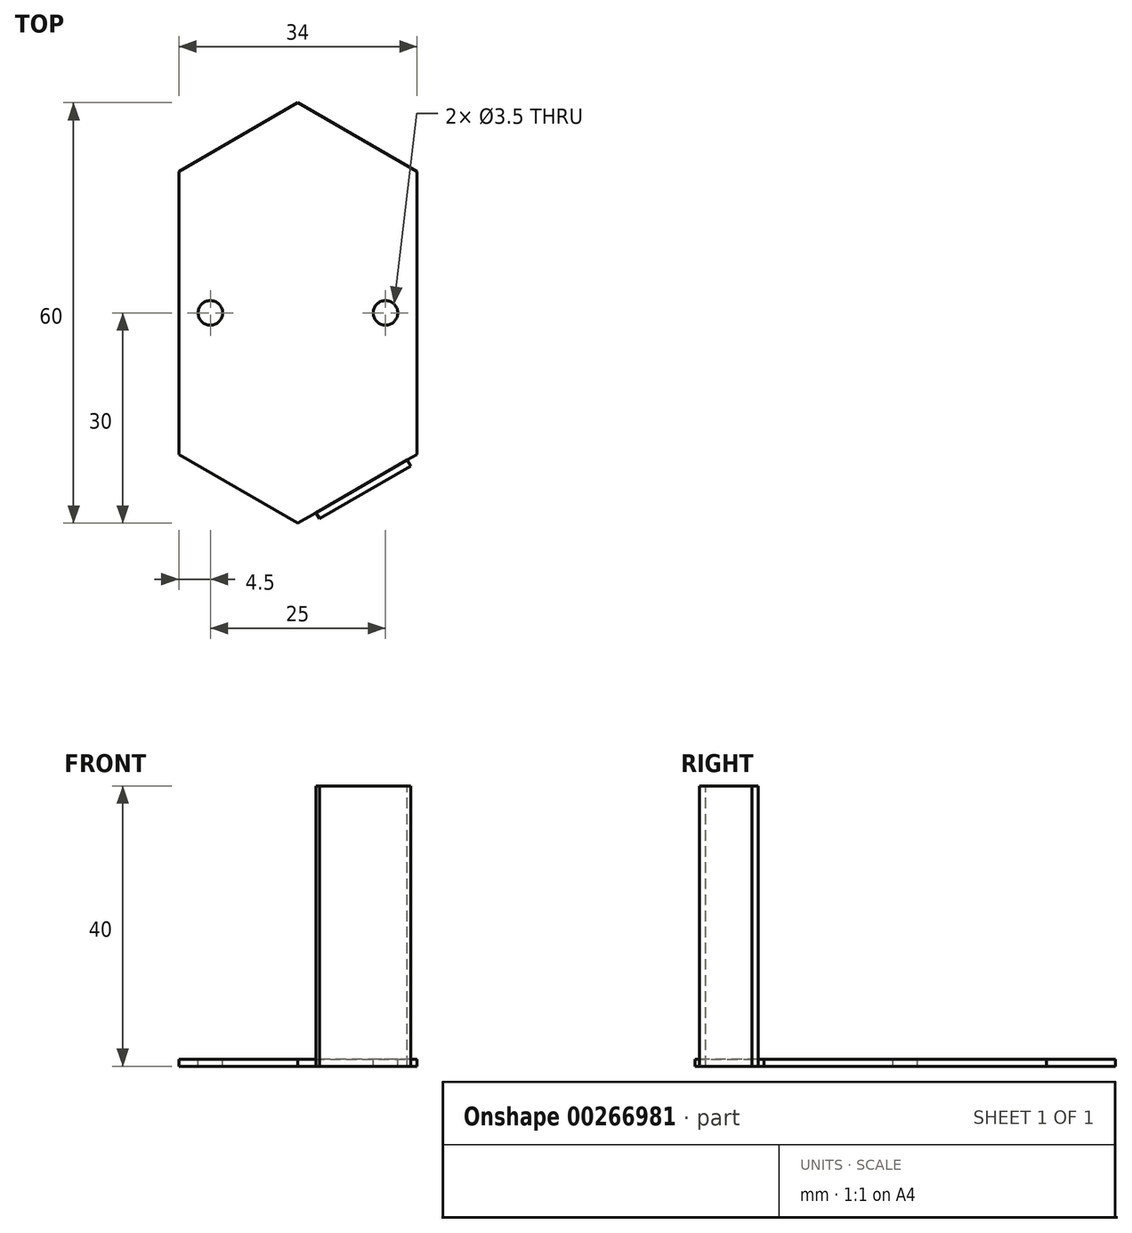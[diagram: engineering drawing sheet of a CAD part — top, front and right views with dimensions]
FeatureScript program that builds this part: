
annotation { "Feature Type Name" : "Feature", "Feature Type Description" : "" }
export const myFeature = defineFeature(function(context is Context, id is Id, definition is map)
    precondition{}
    {
        {
            var Q0;
            Q0=qCreatedBy(makeId("Top.planeOp"),FACE);
            var sketch = newSketch(context, id + "F0", { "sketchPlane" : qUnion([Q0])});
            skCircle(sketch, "E0.cCircle", {"center": v(0, 0) * mm, "radius": 25.98 * mm, "construction": true});
            skLineSegment(sketch, "E0.0", {"start": v(25.98, 15) * mm, "end": v(25.98, -15) * mm});
            skLineSegment(sketch, "E0.1", {"start": v(25.98, -15) * mm, "end": v(0, -30) * mm});
            skLineSegment(sketch, "E0.2", {"start": v(0, -30) * mm, "end": v(-25.98, -15) * mm});
            skLineSegment(sketch, "E0.3", {"start": v(-25.98, -15) * mm, "end": v(-25.98, 15) * mm});
            skLineSegment(sketch, "E0.4", {"start": v(-25.98, 15) * mm, "end": v(0, 30) * mm});
            skLineSegment(sketch, "E0.5", {"start": v(0, 30) * mm, "end": v(25.98, 15) * mm});
            skPoint(sketch, "E0.0.midPoint", {"position": v(25.98, 0) * mm});
            skSolve(sketch);
        }
        {
            var Q0;
            Q0 = qSketchRegion(id + "F0", true);
            extrude(context, id + "F1", {"entities" : qUnion([Q0]), "depth" : 1 * mm});
        }
        {
            var Q0;
            Q0=makeQuery(id+"F1.opExtrude","SWEPT_FACE",FACE,{"disambiguationData":[OSD([sQuery(id+"F0.wireOp",EDGE,"E0.1")])]});
            var sketch = newSketch(context, id + "F2", { "sketchPlane" : qUnion([Q0])});
            skLineSegment(sketch, "E1.bottom", {"start": v(-12, 0) * mm, "end": v(3, 0) * mm});
            skLineSegment(sketch, "E1.top", {"start": v(-12, 40) * mm, "end": v(3, 40) * mm});
            skLineSegment(sketch, "E1.left", {"start": v(-12, 0) * mm, "end": v(-12, 40) * mm});
            skLineSegment(sketch, "E1.right", {"start": v(3, 0) * mm, "end": v(3, 40) * mm});
            skSolve(sketch);
        }
        {
            var Q0;
            Q0 = qSketchRegion(id + "F2", true);
            extrude(context, id + "F3", {"entities" : qUnion([Q0]), "depth" : 1 * mm});
        }
        {
            var Q0;
            Q0=makeQuery(id+"F1.opExtrude","CAP_FACE",FACE,{"disambiguationData":[OSD([sQuery(id+"F0.wireOp",EDGE,"E0.0"),sQuery(id+"F0.wireOp",EDGE,"E0.1"),sQuery(id+"F0.wireOp",EDGE,"E0.2"),sQuery(id+"F0.wireOp",EDGE,"E0.3"),sQuery(id+"F0.wireOp",EDGE,"E0.4"),sQuery(id+"F0.wireOp",EDGE,"E0.5")])],"isStart":false});
            var sketch = newSketch(context, id + "F4", { "sketchPlane" : qUnion([Q0])});
            skLineSegment(sketch, "E2.bottom", {"start": v(-32, 25) * mm, "end": v(-17, 25) * mm});
            skLineSegment(sketch, "E2.top", {"start": v(-32, -25) * mm, "end": v(-17, -25) * mm});
            skLineSegment(sketch, "E2.left", {"start": v(-32, 25) * mm, "end": v(-32, -25) * mm});
            skLineSegment(sketch, "E2.right", {"start": v(-17, 25) * mm, "end": v(-17, -25) * mm});
            skLineSegment(sketch, "E3.MirrorCS", {"start": v(32, 25) * mm, "end": v(17, 25) * mm});
            skLineSegment(sketch, "E4.MirrorCS", {"start": v(32, -25) * mm, "end": v(17, -25) * mm});
            skLineSegment(sketch, "E5.MirrorCS", {"start": v(17, 25) * mm, "end": v(17, -25) * mm});
            skLineSegment(sketch, "E6.MirrorCS", {"start": v(32, 25) * mm, "end": v(32, -25) * mm});
            skSolve(sketch);
        }
        {
            var Q0;
            Q0 = qSketchRegion(id + "F4", true);
            extrude(context, id + "F5", {"entities" : qUnion([Q0]), "operationType" : NewBodyOperationType.REMOVE, "oppositeDirection" : true, "depth" : 25 * mm});
        }
        {
            var Q0;
            Q0=makeQuery(id+"F1.opExtrude","CAP_FACE",FACE,{"disambiguationData":[OSD([sQuery(id+"F0.wireOp",EDGE,"E0.0"),sQuery(id+"F0.wireOp",EDGE,"E0.1"),sQuery(id+"F0.wireOp",EDGE,"E0.2"),sQuery(id+"F0.wireOp",EDGE,"E0.3"),sQuery(id+"F0.wireOp",EDGE,"E0.4"),sQuery(id+"F0.wireOp",EDGE,"E0.5")])],"isStart":false});
            var sketch = newSketch(context, id + "F6", { "sketchPlane" : qUnion([Q0])});
            skPoint(sketch, "E7", {"position": v(12.5, 0) * mm});
            skPoint(sketch, "E8", {"position": v(-12.5, 0) * mm});
            skSolve(sketch);
        }
        {
            var Q0;
            Q0=sQuery(id+"F6.wireOp",VERTEX,"E7");
            var Q1;
            Q1=sQuery(id+"F6.wireOp",VERTEX,"E8");
            var Q2;
            Q2=makeQuery(id+"F1.opExtrude","SWEPT_BODY",BODY,{"disambiguationData":[OSD([sQuery(id+"F0.wireOp",EDGE,"E0.0"),sQuery(id+"F0.wireOp",EDGE,"E0.1"),sQuery(id+"F0.wireOp",EDGE,"E0.2"),sQuery(id+"F0.wireOp",EDGE,"E0.3"),sQuery(id+"F0.wireOp",EDGE,"E0.4"),sQuery(id+"F0.wireOp",EDGE,"E0.5")])]});
            hole(context, id + "F7", {"style" : HoleStyle.SIMPLE, "endStyle" : HoleEndStyle.THROUGH, "holeDiameter" : 3.5 * mm, "tappedDepth" : 12 * mm, "tapClearance" : 3, "locations" : qUnion([Q0, Q1]), "scope" : qUnion([Q2])});
        }
    });
